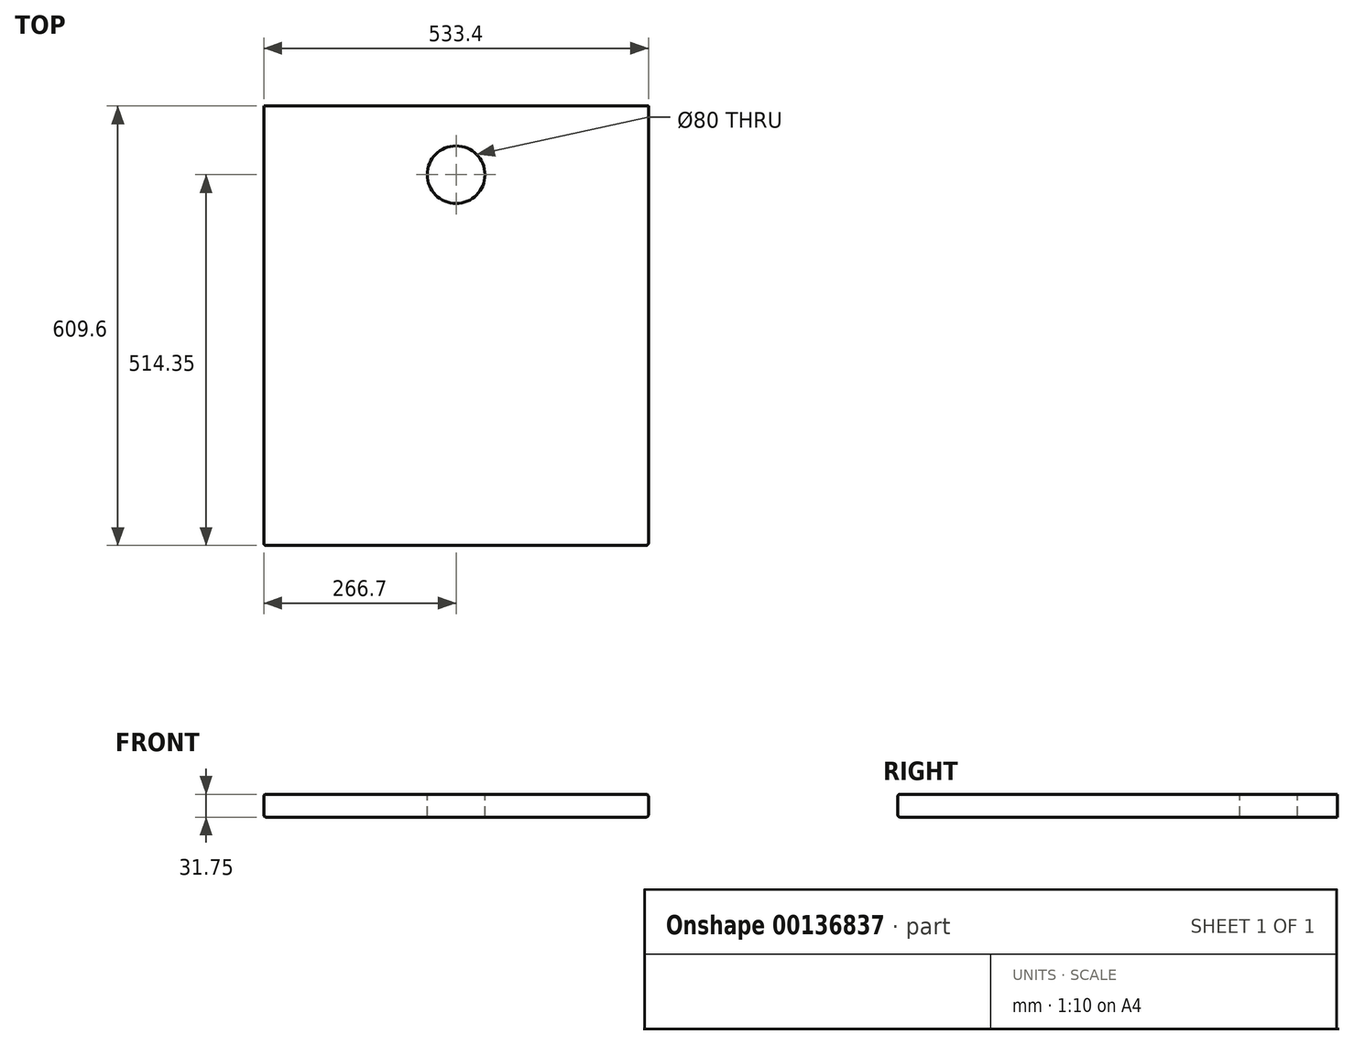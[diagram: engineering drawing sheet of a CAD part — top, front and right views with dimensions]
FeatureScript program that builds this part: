
annotation { "Feature Type Name" : "Feature", "Feature Type Description" : "" }
export const myFeature = defineFeature(function(context is Context, id is Id, definition is map)
    precondition{}
    {
        {
            var Q0;
            Q0=qCreatedBy(makeId("Top.planeOp"),FACE);
            var sketch = newSketch(context, id + "F0", { "sketchPlane" : qUnion([Q0])});
            skLineSegment(sketch, "E0.bottom", {"start": v(266.7, -304.8) * mm, "end": v(-266.7, -304.8) * mm});
            skLineSegment(sketch, "E0.top", {"start": v(266.7, 304.8) * mm, "end": v(-266.7, 304.8) * mm});
            skLineSegment(sketch, "E0.left", {"start": v(266.7, -304.8) * mm, "end": v(266.7, 304.8) * mm});
            skLineSegment(sketch, "E0.right", {"start": v(-266.7, -304.8) * mm, "end": v(-266.7, 304.8) * mm});
            skPoint(sketch, "E0.middle", {"position": v(0, 0) * mm});
            skSolve(sketch);
        }
        {
            var Q0;
            Q0=makeQuery(id+"F0.imprint","IMPRINT",FACE,{"disambiguationData":[TD([[makeQuery(id+"F0.imprint","IMPRINT",EDGE,{"derivedFrom":sQuery(id+"F0.wireOp",EDGE,"E0.bottom")}),-1.0]])]});
            extrude(context, id + "F1", {"entities" : qUnion([Q0]), "depth" : 31.75 * mm});
        }
        {
            var Q0;
            Q0=makeQuery(id+"F1.opExtrude","CAP_EDGE",EDGE,{"disambiguationData":[OSD([sQuery(id+"F0.wireOp",EDGE,"E0.bottom")])],"isStart":false});
            var Q1;
            Q1=makeQuery(id+"F1.opExtrude","CAP_EDGE",EDGE,{"disambiguationData":[OSD([sQuery(id+"F0.wireOp",EDGE,"E0.right")])],"isStart":false});
            var Q2;
            Q2=makeQuery(id+"F1.opExtrude","CAP_EDGE",EDGE,{"disambiguationData":[OSD([sQuery(id+"F0.wireOp",EDGE,"E0.left")])],"isStart":false});
            var Q3;
            Q3=makeQuery(id+"F1.opExtrude","CAP_EDGE",EDGE,{"disambiguationData":[OSD([sQuery(id+"F0.wireOp",EDGE,"E0.left")])],"isStart":true});
            var Q4;
            Q4=makeQuery(id+"F1.opExtrude","CAP_EDGE",EDGE,{"disambiguationData":[OSD([sQuery(id+"F0.wireOp",EDGE,"E0.bottom")])],"isStart":true});
            var Q5;
            Q5=makeQuery(id+"F1.opExtrude","CAP_EDGE",EDGE,{"disambiguationData":[OSD([sQuery(id+"F0.wireOp",EDGE,"E0.right")])],"isStart":true});
            var Q6;
            Q6=makeQuery(id+"F1.opExtrude","SWEPT_EDGE",EDGE,{"disambiguationData":[OSD([sQuery(id+"F0.wireOp",EDGE,"E0.bottom"),sQuery(id+"F0.wireOp",EDGE,"E0.right")])]});
            var Q7;
            Q7=makeQuery(id+"F1.opExtrude","SWEPT_EDGE",EDGE,{"disambiguationData":[OSD([sQuery(id+"F0.wireOp",EDGE,"E0.bottom"),sQuery(id+"F0.wireOp",EDGE,"E0.left")])]});
            fillet(context, id + "F2", {"entities" : qUnion([Q0, Q1, Q2, Q3, Q4, Q5, Q6, Q7]), "radius" : 3.17 * mm, "tangentPropagation" : true, "allowEdgeOverflow" : false});
        }
        {
            var Q0;
            Q0=makeQuery(id+"F1.opExtrude","CAP_FACE",FACE,{"disambiguationData":[OSD([sQuery(id+"F0.wireOp",EDGE,"E0.bottom"),sQuery(id+"F0.wireOp",EDGE,"E0.top"),sQuery(id+"F0.wireOp",EDGE,"E0.left"),sQuery(id+"F0.wireOp",EDGE,"E0.right")])],"isStart":false});
            var sketch = newSketch(context, id + "F3", { "sketchPlane" : qUnion([Q0])});
            skCircle(sketch, "E1", {"center": v(0, 209.55) * mm, "radius": 40 * mm});
            skSolve(sketch);
        }
        {
            var Q0;
            Q0=makeQuery(id+"F3.imprint","IMPRINT",FACE,{"disambiguationData":[TD([[makeQuery(id+"F3.imprint","IMPRINT",EDGE,{"derivedFrom":sQuery(id+"F3.wireOp",EDGE,"E1")}),1.0]])]});
            extrude(context, id + "F4", {"entities" : qUnion([Q0]), "operationType" : NewBodyOperationType.REMOVE, "endBound" : BoundingType.THROUGH_ALL, "oppositeDirection" : true, "depth" : 25.4 * mm});
        }
    });
